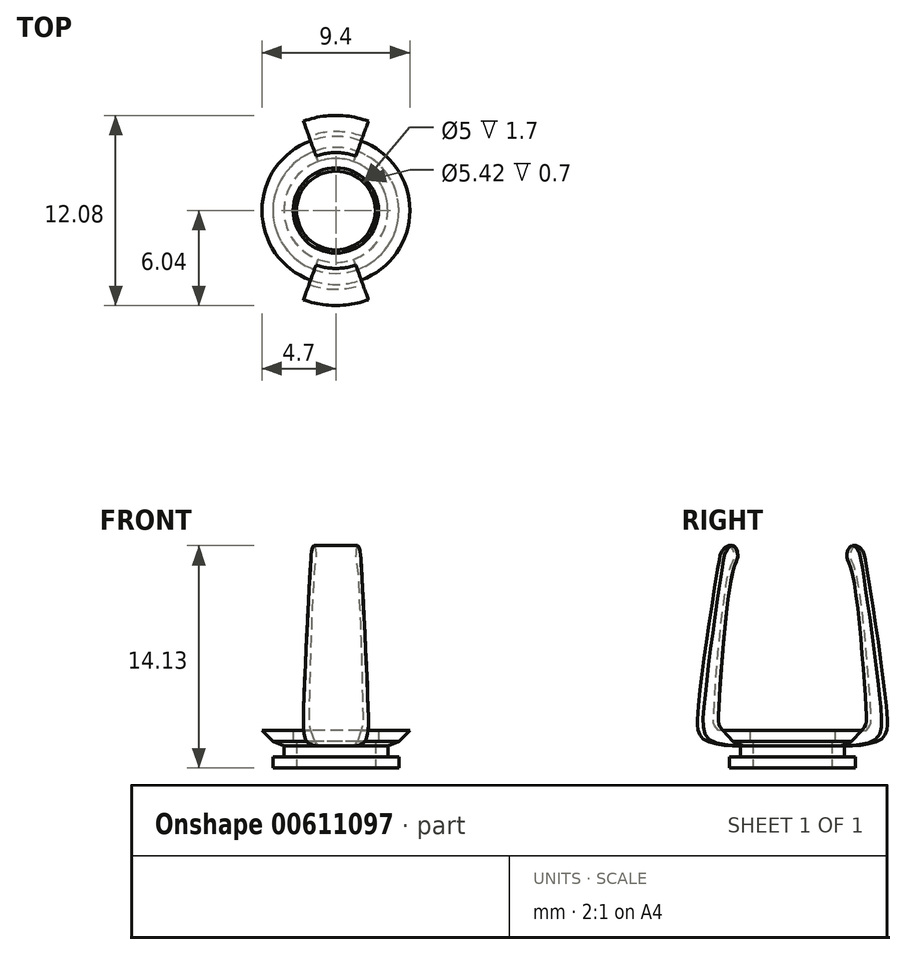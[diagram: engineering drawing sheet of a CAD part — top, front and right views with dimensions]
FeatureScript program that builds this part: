
annotation { "Feature Type Name" : "Feature", "Feature Type Description" : "" }
export const myFeature = defineFeature(function(context is Context, id is Id, definition is map)
    precondition{}
    {
        {
            var Q0;
            Q0=qCreatedBy(makeId("Top.planeOp"),FACE);
            var sketch = newSketch(context, id + "F0", { "sketchPlane" : qUnion([Q0])});
            skCircle(sketch, "E0", {"center": v(0, 0) * mm, "radius": 2.5 * mm});
            skCircle(sketch, "E1", {"center": v(0, 0) * mm, "radius": 4 * mm});
            skPoint(sketch, "E2", {"position": v(-4, 0) * mm});
            skPoint(sketch, "E3", {"position": v(-2.5, 0) * mm});
            skPoint(sketch, "E4", {"position": v(0, -2.5) * mm});
            skPoint(sketch, "E5", {"position": v(0, -4) * mm});
            skSolve(sketch);
        }
        {
            var Q0;
            Q0=makeQuery(id+"F0.imprint","IMPRINT",FACE,{"disambiguationData":[TD([[makeQuery(id+"F0.imprint","IMPRINT",EDGE,{"derivedFrom":sQuery(id+"F0.wireOp",EDGE,"E0")}),-1.0]])]});
            extrude(context, id + "F1", {"entities" : qUnion([Q0]), "depth" : 0.7 * mm, "offsetDistance" : 25 * mm});
        }
        {
            var Q0;
            Q0=makeQuery(id+"F1.opExtrude","CAP_FACE",FACE,{"disambiguationData":[OSD([sQuery(id+"F0.wireOp",EDGE,"E0"),sQuery(id+"F0.wireOp",EDGE,"E1")])],"isStart":false});
            var sketch = newSketch(context, id + "F2", { "sketchPlane" : qUnion([Q0])});
            skCircle(sketch, "E6", {"center": v(0, 0) * mm, "radius": 2.5 * mm});
            skCircle(sketch, "E7", {"center": v(0, 0) * mm, "radius": 3.3 * mm});
            skSolve(sketch);
        }
        {
            var Q0;
            Q0=makeQuery(id+"F2.imprint","IMPRINT",FACE,{"disambiguationData":[TD([[makeQuery(id+"F2.imprint","IMPRINT",EDGE,{"derivedFrom":sQuery(id+"F2.wireOp",EDGE,"E6")}),-1.0]])]});
            extrude(context, id + "F3", {"entities" : qUnion([Q0]), "operationType" : NewBodyOperationType.ADD, "depth" : 1 * mm, "offsetDistance" : 25 * mm});
        }
        {
            var Q0;
            Q0=makeQuery(id+"F3.opExtrude","CAP_FACE",FACE,{"disambiguationData":[OSD([sQuery(id+"F2.wireOp",EDGE,"E6"),sQuery(id+"F2.wireOp",EDGE,"E7")])],"isStart":false});
            var sketch = newSketch(context, id + "F4", { "sketchPlane" : qUnion([Q0])});
            skCircle(sketch, "E8", {"center": v(0, 0) * mm, "radius": 2.7 * mm});
            skCircle(sketch, "E9", {"center": v(0, 0) * mm, "radius": 4 * mm});
            skSolve(sketch);
        }
        {
            var Q0;
            Q0 = qSketchRegion(id + "F4", true);
            extrude(context, id + "F5", {"entities" : qUnion([Q0]), "operationType" : NewBodyOperationType.ADD, "depth" : 0.7 * mm, "offsetDistance" : 25 * mm});
        }
        {
            var Q0;
            Q0=qCreatedBy(makeId("Right.planeOp"),FACE);
            var sketch = newSketch(context, id + "F6", { "sketchPlane" : qUnion([Q0])});
            skLineSegment(sketch, "E10", {"start": v(-4, 2.4) * mm, "end": v(-4.7, 2.4) * mm});
            skLineSegment(sketch, "E11", {"start": v(-4.7, 2.4) * mm, "end": v(-4, 1.7) * mm});
            skLineSegment(sketch, "E12", {"start": v(-4, 1.7) * mm, "end": v(-4, 2.4) * mm});
            skLineSegment(sketch, "E13", {"start": v(-4, 1.7) * mm, "end": v(-3.3, 1.4) * mm});
            skLineSegment(sketch, "E14", {"start": v(-3.3, 1.4) * mm, "end": v(-3.3, 1.7) * mm});
            skLineSegment(sketch, "E15", {"start": v(-3.3, 1.7) * mm, "end": v(-4, 1.7) * mm});
            skSolve(sketch);
        }
        {
            var Q0;
            Q0=makeQuery(id+"F6.imprint","IMPRINT",FACE,{"disambiguationData":[TD([[makeQuery(id+"F6.imprint","IMPRINT",EDGE,{"derivedFrom":sQuery(id+"F6.wireOp",EDGE,"E10")}),1.0]])]});
            var Q1;
            Q1=makeQuery(id+"F6.imprint","IMPRINT",FACE,{"disambiguationData":[TD([[makeQuery(id+"F6.imprint","IMPRINT",EDGE,{"derivedFrom":sQuery(id+"F6.wireOp",EDGE,"E13")}),1.0]])]});
            var Q2;
            Q2=makeQuery(id+"F5.opExtrude","CAP_EDGE",EDGE,{"disambiguationData":[OSD([sQuery(id+"F4.wireOp",EDGE,"E8")])],"isStart":false});
            revolve(context, id + "F7", {"operationType" : NewBodyOperationType.ADD, "entities" : qUnion([Q0, Q1]), "axis" : qUnion([Q2]), "revolveType" : RevolveType.FULL});
        }
        {
            var Q0;
            Q0=qCreatedBy(makeId("Right.planeOp"),FACE);
            var sketch = newSketch(context, id + "F8", { "sketchPlane" : qUnion([Q0])});
            skFitSpline(sketch, "E16", {"points": [v(-3.3, 1.4) * mm, v(-6, 3.57) * mm, v(-4.68, 13.06) * mm, v(-4.4, 13.9) * mm, v(-3.97, 14.12) * mm, v(-3.68, 13.48) * mm, v(-4, 12.57) * mm, v(-5, 3.17) * mm, v(-4.7, 2.4) * mm], "startDerivative": vector(-54.92, 0.71) * mm, "endDerivative": vector(11.7, -13.34) * mm});
            skLineSegment(sketch, "E17", {"start": v(-4.7, 2.4) * mm, "end": v(-4, 1.7) * mm});
            skLineSegment(sketch, "E18", {"start": v(-4, 1.7) * mm, "end": v(-3.3, 1.4) * mm});
            skSolve(sketch);
        }
        {
            var Q0;
            Q0=makeQuery(id+"F8.imprint","IMPRINT",FACE,{"disambiguationData":[TD([[makeQuery(id+"F8.imprint","IMPRINT",EDGE,{"derivedFrom":sQuery(id+"F8.wireOp",EDGE,"E16")}),-1.0]])]});
            var Q1;
            Q1=sQuery(id+"F8.wireOp",EDGE,"E16");
            var Q2;
            Q2=makeQuery(id+"F7.opRevolve","SWEPT_EDGE",EDGE,{"disambiguationData":[OSD([sQuery(id+"F6.wireOp",EDGE,"E10"),sQuery(id+"F6.wireOp",EDGE,"E11")])]});
            revolve(context, id + "F9", {"operationType" : NewBodyOperationType.ADD, "entities" : qUnion([Q0]), "surfaceEntities" : qUnion([Q1]), "axis" : qUnion([Q2]), "revolveType" : RevolveType.SYMMETRIC, "angle" : 40 * degree});
        }
        {
            var Q0;
            Q0=makeQuery(id+"F1.opExtrude","SWEPT_BODY",BODY,{"disambiguationData":[OSD([sQuery(id+"F0.wireOp",EDGE,"E0"),sQuery(id+"F0.wireOp",EDGE,"E1")])]});
            var Q1;
            Q1=qCreatedBy(makeId("Front.planeOp"),FACE);
            mirror(context, id + "F10", {"operationType" : NewBodyOperationType.ADD, "entities" : qUnion([Q0]), "mirrorPlane" : qUnion([Q1])});
        }
    });
